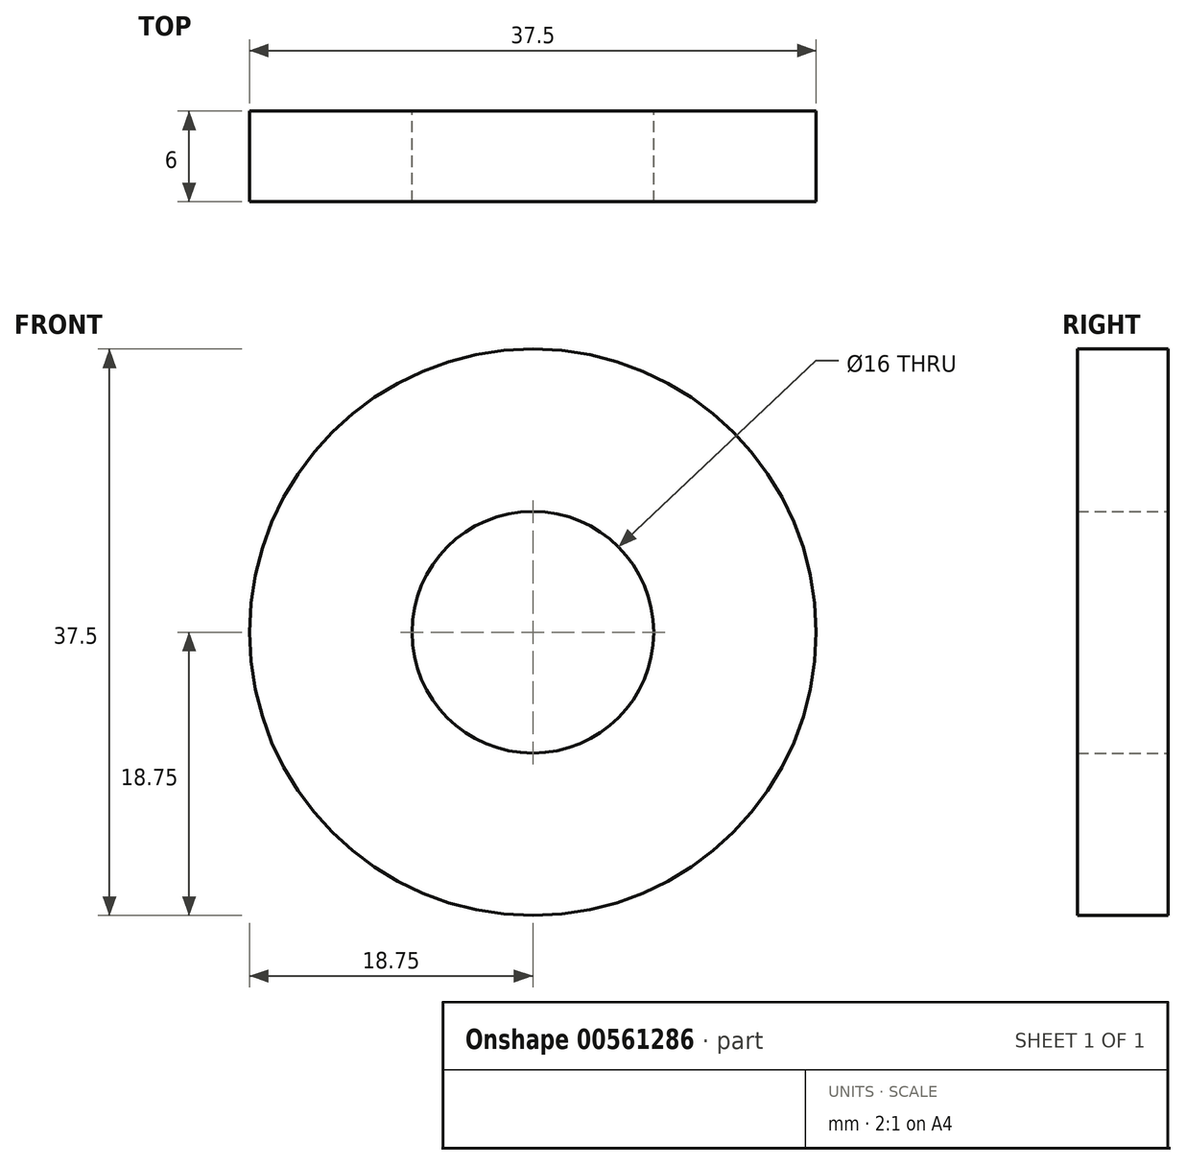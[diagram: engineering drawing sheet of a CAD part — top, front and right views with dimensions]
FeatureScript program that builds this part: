
annotation { "Feature Type Name" : "Feature", "Feature Type Description" : "" }
export const myFeature = defineFeature(function(context is Context, id is Id, definition is map)
    precondition{}
    {
        {
            var Q0;
            Q0=qCreatedBy(makeId("Front.planeOp"),FACE);
            var sketch = newSketch(context, id + "F0", { "sketchPlane" : qUnion([Q0])});
            skCircle(sketch, "E0", {"center": v(0, 0) * mm, "radius": 18.75 * mm});
            skCircle(sketch, "E1", {"center": v(0, 0) * mm, "radius": 8 * mm});
            skSolve(sketch);
        }
        {
            var Q0;
            Q0 = qSketchRegion(id + "F0", true);
            extrude(context, id + "F1", {"entities" : qUnion([Q0]), "depth" : 6 * mm, "offsetDistance" : 25 * mm});
        }
    });
